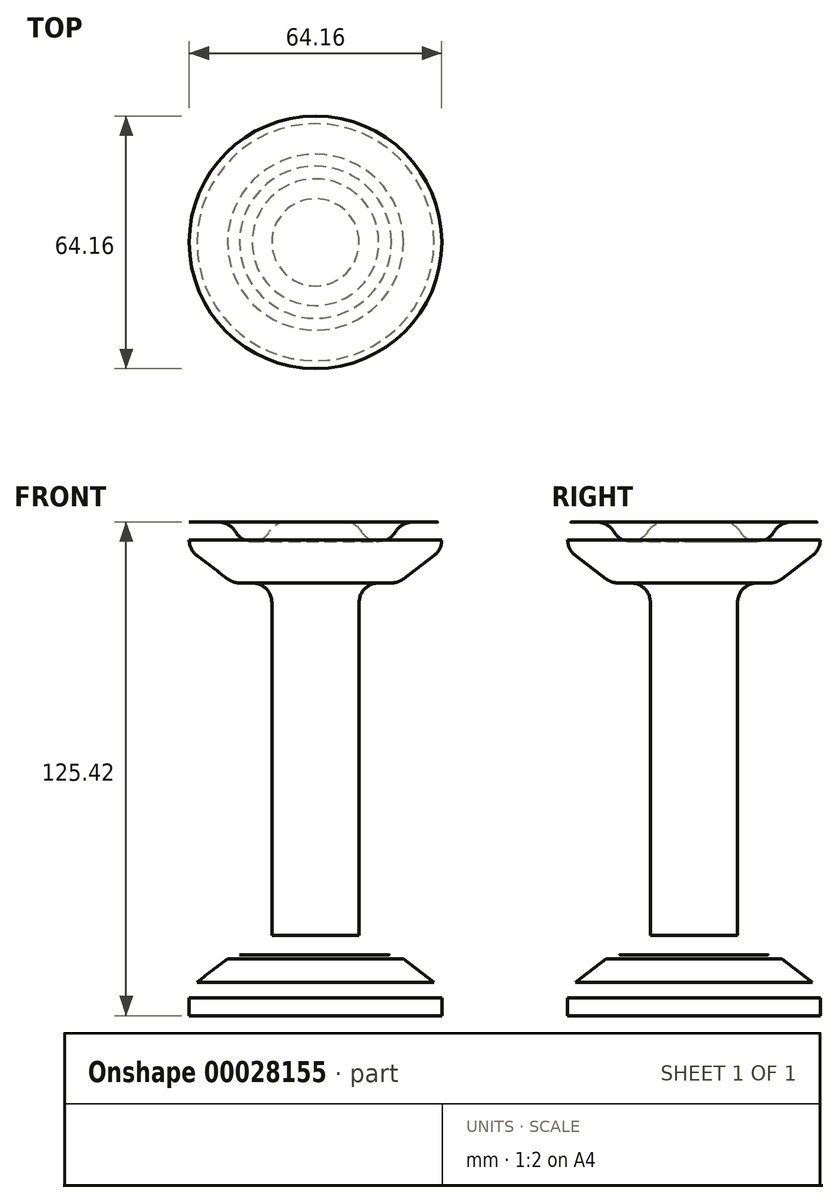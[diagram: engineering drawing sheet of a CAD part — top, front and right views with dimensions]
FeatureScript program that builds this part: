
annotation { "Feature Type Name" : "Feature", "Feature Type Description" : "" }
export const myFeature = defineFeature(function(context is Context, id is Id, definition is map)
    precondition{}
    {
        {
            var Q0;
            Q0=qCreatedBy(makeId("Front.planeOp"),FACE);
            var sketch = newSketch(context, id + "F0", { "sketchPlane" : qUnion([Q0])});
            skLineSegment(sketch, "E0", {"start": v(0, 62.7) * mm, "end": v(-7.43, 62.7) * mm});
            skLineSegment(sketch, "E1", {"start": v(-32.08, 62.7) * mm, "end": v(-32.08, 58.18) * mm});
            skLineSegment(sketch, "E2", {"start": v(-30.12, 54.2) * mm, "end": v(-22.34, 48.28) * mm});
            skLineSegment(sketch, "E3", {"start": v(-19.31, 47.25) * mm, "end": v(-16.08, 47.25) * mm});
            skLineSegment(sketch, "E4", {"start": v(-11.08, 42.25) * mm, "end": v(-11.08, 0) * mm});
            skLineSegment(sketch, "E5.MirrorCS", {"start": v(-30.12, -54.2) * mm, "end": v(-22.34, -48.28) * mm});
            skLineSegment(sketch, "E6.MirrorCS", {"start": v(-32.08, -62.7) * mm, "end": v(-32.08, -58.18) * mm});
            skLineSegment(sketch, "E7.MirrorCS", {"start": v(-11.08, -42.25) * mm, "end": v(-11.08, 0) * mm});
            skLineSegment(sketch, "E8.MirrorCS", {"start": v(-19.31, -47.25) * mm, "end": v(-16.08, -47.25) * mm});
            skLineSegment(sketch, "E9.MirrorCS", {"start": v(0, -62.7) * mm, "end": v(-32.08, -62.7) * mm});
            skPoint(sketch, "E10.orphan", {"position": v(-42.56, 0) * mm});
            skArc(sketch, "E11", {"start": v(-20.33, 60.22) * mm, "mid": v(-16.04, 57.75) * mm, "end": v(-11.75, 60.22) * mm});
            skLineSegment(sketch, "E12.trimOffspring", {"start": v(-24.65, 62.7) * mm, "end": v(-32.08, 62.7) * mm});
            skPoint(sketch, "E13.visualSharp", {"position": v(-21, 62.7) * mm});
            skArc(sketch, "E13.filletArc", {"start": v(-20.33, 60.22) * mm, "mid": v(-22.16, 62.04) * mm, "end": v(-24.65, 62.7) * mm});
            skPoint(sketch, "E14.visualSharp", {"position": v(-11.08, 62.7) * mm});
            skArc(sketch, "E14.filletArc", {"start": v(-7.43, 62.7) * mm, "mid": v(-9.92, 62.04) * mm, "end": v(-11.75, 60.22) * mm});
            skPoint(sketch, "E15.visualSharp", {"position": v(-32.08, 55.7) * mm});
            skArc(sketch, "E15.filletArc", {"start": v(-32.08, 58.18) * mm, "mid": v(-31.56, 55.96) * mm, "end": v(-30.12, 54.2) * mm});
            skPoint(sketch, "E16.visualSharp", {"position": v(-21, 47.25) * mm});
            skArc(sketch, "E16.filletArc", {"start": v(-22.34, 48.28) * mm, "mid": v(-20.91, 47.51) * mm, "end": v(-19.31, 47.25) * mm});
            skPoint(sketch, "E17.visualSharp", {"position": v(-11.08, 47.25) * mm});
            skArc(sketch, "E17.filletArc", {"start": v(-11.08, 42.25) * mm, "mid": v(-12.55, 45.79) * mm, "end": v(-16.08, 47.25) * mm});
            skPoint(sketch, "E18.visualSharp", {"position": v(-32.08, -55.7) * mm});
            skArc(sketch, "E18.filletArc", {"start": v(-30.12, -54.2) * mm, "mid": v(-31.56, -55.96) * mm, "end": v(-32.08, -58.18) * mm});
            skPoint(sketch, "E19.visualSharp", {"position": v(-21, -47.25) * mm});
            skArc(sketch, "E19.filletArc", {"start": v(-19.31, -47.25) * mm, "mid": v(-20.91, -47.51) * mm, "end": v(-22.34, -48.28) * mm});
            skPoint(sketch, "E20.visualSharp", {"position": v(-11.08, -47.25) * mm});
            skArc(sketch, "E20.filletArc", {"start": v(-16.08, -47.25) * mm, "mid": v(-12.55, -45.79) * mm, "end": v(-11.08, -42.25) * mm});
            skSolve(sketch);
        }
        {
            var Q0;
            Q0=qCreatedBy(makeId("Front.planeOp"),FACE);
            var sketch = newSketch(context, id + "F1", { "sketchPlane" : qUnion([Q0])});
            skLineSegment(sketch, "E21", {"start": v(0, 62.54) * mm, "end": v(0, -62.95) * mm});
            skSolve(sketch);
        }
        {
            var Q0;
            Q0=sQuery(id+"F0.wireOp",EDGE,"E9.MirrorCS");
            var Q1;
            Q1=sQuery(id+"F0.wireOp",EDGE,"E8.MirrorCS");
            var Q2;
            Q2=sQuery(id+"F0.wireOp",EDGE,"E5.MirrorCS");
            var Q3;
            Q3=sQuery(id+"F0.wireOp",EDGE,"E7.MirrorCS");
            var Q4;
            Q4=sQuery(id+"F0.wireOp",EDGE,"E6.MirrorCS");
            var Q5;
            Q5=sQuery(id+"F0.wireOp",EDGE,"E4");
            var Q6;
            Q6=sQuery(id+"F0.wireOp",EDGE,"E3");
            var Q7;
            Q7=sQuery(id+"F0.wireOp",EDGE,"E0");
            var Q8;
            Q8=sQuery(id+"F0.wireOp",EDGE,"E2");
            var Q9;
            Q9=sQuery(id+"F0.wireOp",EDGE,"E12.trimOffspring");
            var Q10;
            Q10=sQuery(id+"F0.wireOp",EDGE,"E13.filletArc");
            var Q11;
            Q11=sQuery(id+"F0.wireOp",EDGE,"E11");
            var Q12;
            Q12=sQuery(id+"F0.wireOp",EDGE,"E14.filletArc");
            var Q13;
            Q13=sQuery(id+"F0.wireOp",EDGE,"E15.filletArc");
            var Q14;
            Q14=sQuery(id+"F0.wireOp",EDGE,"E16.filletArc");
            var Q15;
            Q15=sQuery(id+"F0.wireOp",EDGE,"E17.filletArc");
            var Q16;
            Q16=sQuery(id+"F1.wireOp",EDGE,"E21");
            revolve(context, id + "F2", {"bodyType" : ToolBodyType.SURFACE, "surfaceEntities" : qUnion([Q0, Q1, Q2, Q3, Q4, Q5, Q6, Q7, Q8, Q9, Q10, Q11, Q12, Q13, Q14, Q15]), "axis" : qUnion([Q16]), "revolveType" : RevolveType.FULL});
        }
    });
